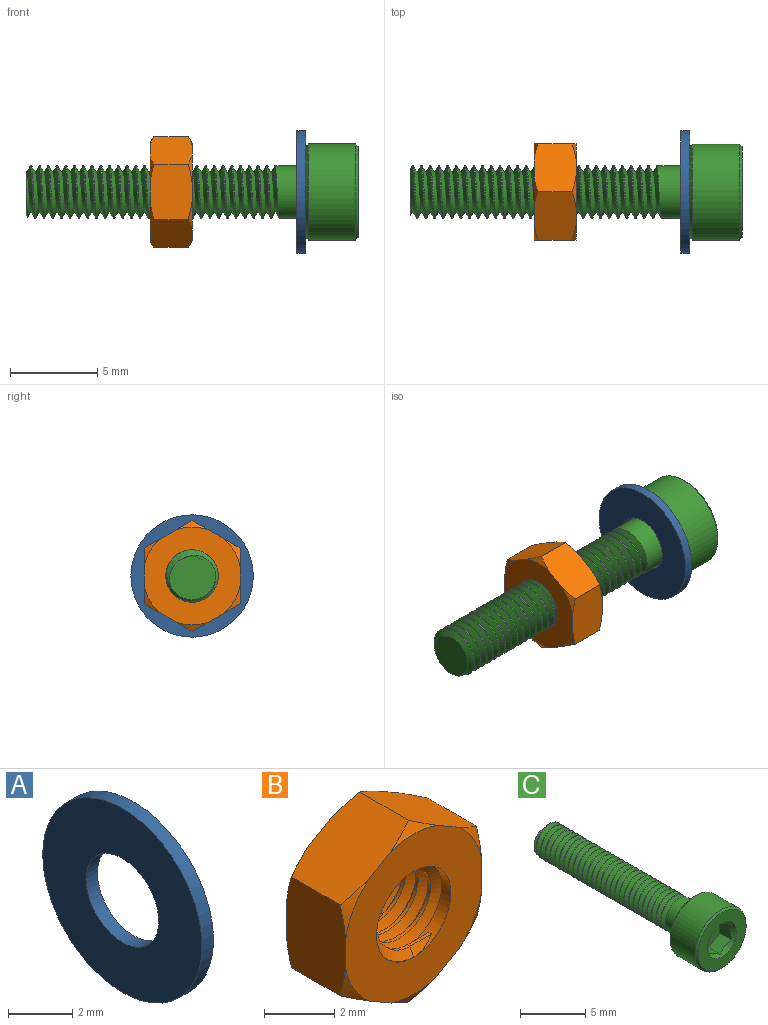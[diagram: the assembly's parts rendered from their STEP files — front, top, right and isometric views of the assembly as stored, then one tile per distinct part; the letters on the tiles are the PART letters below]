
ASSEMBLY  parts=3 mates=2
PART A: 4 faces, bbox 0.5x7x7 mm
  f0: plane 7x7mm, normal (-1,0,0), area 30.4mm2, adj f1,f3
  f1: cylinder r=1.6mm len=3.2mm, axis (1,0,0), area 5mm2, adj f0,f2
  f2: plane 7x7mm, normal (1,0,0), area 30.4mm2, adj f1,f3
  f3: cylinder r=3.5mm len=7mm, axis (1,0,0), area 11mm2, adj f0,f2
PART B: 28 faces, bbox 6.4x2.6x6.5 mm
  f0: cone r=2.8mm half-angle=60deg, axis (0,-1,0), area 0.4mm2, adj f11,f22,f23
  f1: cone r=2.8mm half-angle=60deg, axis (0,-1,0), area 0.4mm2, adj f11,f23,f24
  f2: cone r=2.8mm half-angle=60deg, axis (0,-1,0), area 0.4mm2, adj f11,f24,f25
  f3: cone r=2.8mm half-angle=60deg, axis (0,-1,0), area 0.4mm2, adj f11,f25,f26
  f4: cone r=2.8mm half-angle=60deg, axis (0,-1,0), area 0.4mm2, adj f11,f22,f27
  f5: cone r=3.18mm half-angle=60deg, axis (0,1,0), area 0.4mm2, adj f10,f22,f23
  f6: cone r=3.18mm half-angle=60deg, axis (0,1,0), area 0.4mm2, adj f10,f23,f24
  f7: cone r=3.18mm half-angle=60deg, axis (0,1,0), area 0.4mm2, adj f10,f24,f25
  f8: cone r=3.18mm half-angle=60deg, axis (0,1,0), area 0.4mm2, adj f10,f25,f26
  f9: cone r=3.18mm half-angle=60deg, axis (0,1,0), area 0.4mm2, adj f10,f26,f27
  f10: plane 5.6x5.5mm, normal (0,-1,0), area 17.4mm2, adj f5,f6,f7,f8,f9,f12,f21,f22
  f11: plane 5.6x5.5mm, normal (0,1,0), area 17.4mm2, adj f0,f1,f2,f3,f4,f12,f20,f22
  f12: cylinder r=1.5mm len=3mm, axis (0,1,0), area 6mm2, adj f10,f11,f13,f15,f16,f17,f18,f19
  f13: plane 0.44x0.25mm, normal (-0.88,0,-0.48), area 0.1mm2, adj f12,f14,f15,f16
  f14: cylinder r=1.21mm len=2.43mm, axis (0,1,0), area 3.3mm2, adj f13,f15,f16,f17
  f15: bspline ~3.46x3mm, area 11mm2, adj f12,f13,f14,f18
  f16: bspline ~3.46x3mm, area 11mm2, adj f12,f13,f14,f19
  f17: plane 0.88x0.11mm, normal (0,0,1), area 0.1mm2, adj f12,f14,f18,f19
  f18: plane 0.96x0.37mm, normal (0,0.87,0.5), area 0.2mm2, adj f12,f15,f17
  f19: plane 0.96x0.37mm, normal (0,-0.87,0.5), area 0.2mm2, adj f12,f16,f17
  f20: cone r=2.8mm half-angle=60deg, axis (0,-1,0), area 0.4mm2, adj f11,f26,f27
  f21: cone r=3.18mm half-angle=60deg, axis (0,1,0), area 0.4mm2, adj f10,f22,f27
  f22: plane 2.87x2.52mm, normal (-0.5,0,0.87), area 7.2mm2, adj f0,f4,f5,f10,f11,f21,f23,f27
  f23: plane 2.87x2.52mm, normal (0.5,0,0.87), area 7.2mm2, adj f0,f1,f5,f6,f10,f11,f22,f24
  f24: plane 3.3x2.52mm, normal (1,0,0), area 7.2mm2, adj f1,f2,f6,f7,f10,f11,f23,f25
  f25: plane 2.87x2.52mm, normal (0.5,0,-0.87), area 7.2mm2, adj f2,f3,f7,f8,f10,f11,f24,f26
  f26: plane 2.87x2.52mm, normal (-0.5,0,-0.87), area 7.2mm2, adj f3,f8,f9,f10,f11,f20,f25,f27
  f27: plane 3.3x2.52mm, normal (-1,0,0), area 7.2mm2, adj f4,f9,f10,f11,f20,f21,f22,f26
PART C: 49 faces, bbox 5.6x19.4x5.6 mm
  f0: cylinder r=1.5mm len=3mm, axis (0,1,0), area 16.3mm2, adj f1,f31,f34,f46,f47,f48
  f1: cylinder r=1.5mm len=3mm, axis (0,1,0), area 0.6mm2, adj f0,f2,f47,f48
  f2: cylinder r=1.5mm len=3mm, axis (0,1,0), area 0.6mm2, adj f1,f3,f47,f48
  f3: cylinder r=1.5mm len=3mm, axis (0,1,0), area 0.6mm2, adj f2,f4,f47,f48
  f4: cylinder r=1.5mm len=3mm, axis (0,1,0), area 0.6mm2, adj f3,f5,f47,f48
  f5: cylinder r=1.5mm len=3mm, axis (0,1,0), area 0.6mm2, adj f4,f6,f47,f48
  f6: cylinder r=1.5mm len=3mm, axis (0,1,0), area 0.6mm2, adj f5,f7,f47,f48
  f7: cylinder r=1.5mm len=3mm, axis (0,1,0), area 0.6mm2, adj f6,f8,f47,f48
  f8: cylinder r=1.5mm len=3mm, axis (0,1,0), area 0.6mm2, adj f7,f9,f47,f48
  f9: cylinder r=1.5mm len=3mm, axis (0,1,0), area 0.6mm2, adj f8,f10,f47,f48
  f10: cylinder r=1.5mm len=3mm, axis (0,1,0), area 0.6mm2, adj f9,f11,f47,f48
  f11: cylinder r=1.5mm len=3mm, axis (0,1,0), area 0.6mm2, adj f10,f12,f47,f48
  f12: cylinder r=1.5mm len=3mm, axis (0,1,0), area 0.6mm2, adj f11,f13,f47,f48
  f13: cylinder r=1.5mm len=3mm, axis (0,1,0), area 0.6mm2, adj f12,f14,f47,f48
  f14: cylinder r=1.5mm len=3mm, axis (0,1,0), area 0.6mm2, adj f13,f15,f47,f48
  f15: cylinder r=1.5mm len=3mm, axis (0,1,0), area 0.6mm2, adj f14,f16,f47,f48
  f16: cylinder r=1.5mm len=3mm, axis (0,1,0), area 0.6mm2, adj f15,f17,f47,f48
  f17: cylinder r=1.5mm len=3mm, axis (0,1,0), area 0.6mm2, adj f16,f18,f47,f48
  f18: cylinder r=1.5mm len=3mm, axis (0,1,0), area 0.6mm2, adj f17,f19,f47,f48
  f19: cylinder r=1.5mm len=3mm, axis (0,1,0), area 0.6mm2, adj f18,f20,f47,f48
  f20: cylinder r=1.5mm len=3mm, axis (0,1,0), area 0.6mm2, adj f19,f21,f47,f48
  f21: cylinder r=1.5mm len=3mm, axis (0,1,0), area 0.6mm2, adj f20,f22,f47,f48
  f22: cylinder r=1.5mm len=3mm, axis (0,1,0), area 0.6mm2, adj f21,f23,f47,f48
  f23: cylinder r=1.5mm len=3mm, axis (0,1,0), area 0.6mm2, adj f22,f24,f47,f48
  f24: cylinder r=1.5mm len=3mm, axis (0,1,0), area 0.6mm2, adj f23,f25,f47,f48
  f25: cylinder r=1.5mm len=3mm, axis (0,1,0), area 0.6mm2, adj f24,f26,f47,f48
  f26: cylinder r=1.5mm len=3mm, axis (0,1,0), area 0.6mm2, adj f25,f27,f47,f48
  f27: cylinder r=1.5mm len=3mm, axis (0,1,0), area 0.6mm2, adj f26,f28,f47,f48
  f28: cylinder r=1.5mm len=3mm, axis (0,1,0), area 0.3mm2, adj f27,f30,f47,f48
  f29: plane 2.75x2.64mm, normal (0,1,0), area 5.2mm2, adj f30,f47,f48
  f30: cone r=1.35mm half-angle=45deg, axis (0,-1,0), area 0.5mm2, adj f28,f29,f47,f48
  f31: plane 1x0.38mm, normal (0,-0.87,-0.5), area 0.3mm2, adj f0,f46,f47
  f32: cylinder r=2.75mm len=5.5mm, axis (0,1,0), area 46.7mm2, adj f44,f45
  f33: plane 5.2x5.2mm, normal (0,-1,0), area 13.5mm2, adj f35,f45
  f34: plane 5.2x5.2mm, normal (0,1,0), area 14.2mm2, adj f0,f44
  f35: cone r=1.57mm half-angle=45deg, axis (0,-1,0), area 3.2mm2, adj f33,f37,f38,f39,f40,f41,f42
  f36: plane 2.89x2.5mm, normal (0,-1,0), area 5.4mm2, adj f37,f38,f39,f40,f41,f42,f43
  f37: plane 1.59x1.52mm, normal (-1,0,0), area 1.8mm2, adj f35,f36,f38,f42
  f38: plane 1.38x1.25mm, normal (-0.5,0,0.87), area 1.8mm2, adj f35,f36,f37,f39
  f39: plane 1.38x1.25mm, normal (0.5,0,0.87), area 1.8mm2, adj f35,f36,f38,f40
  f40: plane 1.45x1.38mm, normal (1,0,0), area 1.8mm2, adj f35,f36,f39,f41
  f41: plane 1.38x1.25mm, normal (0.5,0,-0.87), area 1.8mm2, adj f35,f36,f40,f42
  f42: plane 1.38x1.25mm, normal (-0.5,0,-0.87), area 1.8mm2, adj f35,f36,f37,f41
  f43: cone r=1.57mm half-angle=45deg, axis (0,-1,0), area 0mm2, adj f36
  f44: cone r=2.6mm half-angle=45deg, axis (0,-1,0), area 3.6mm2, adj f32,f34
  f45: cone r=2.75mm half-angle=45deg, axis (0,1,0), area 3.6mm2, adj f32,f33
  f46: plane 1.28x0.4mm, normal (0,0.87,-0.5), area 0.4mm2, adj f0,f31,f48
  f47: bspline ~14.55x3.46mm, area 102.6mm2, adj f0,f1,f2,f3,f4,f5,f6,f7
  f48: bspline ~14.64x3.46mm, area 104mm2, adj f0,f1,f2,f3,f4,f5,f6,f7
PLACE A at identity fixed
PLACE B rot(axis=(0,0,1),90deg) t=(-8.4,0,0)mm
PLACE C rot(axis=(0,0,1),90deg) t=(-15.5,0,0)mm
MATE fastened C.f0 <-> A.f1  axis (1,0,0) through (0.5,0,0)mm
MATE fastened B.f0 <-> A.f1  axis (-1,0,0) through (-6,0,0)mm
